# Revit family: Coffee_Table-Capri-Cumberland
name_source: partatom
category: Furniture
revit_build: Autodesk Revit 2014 (Build: 20130308_1515(x64)
units: mm (PartAtom-declared; Revit-internal decimal feet)

## types (5) — shared parameters
Assembly Code = E2020200
Base Finish = CUM - Powder Coat - Metal White
Glide Finish = CUM - Plastic Black
Keynote = 12500
Leg Finish = CUM - Powder Coat - Metal White
Low Emitting Finish = Yes
Low Emitting Material = Yes
Manufacturer = Cumberland Furniture
Post Finish = CUM - Powder Coat - Metal White
Salvage or Reuse = Yes
Type Comments = Capri
URL = www.cumberlandfurniture.com
zero-valued in all types: Percentage of Recycled Content

## per-type parameters (varying)
| type | Description | Diameter | Height | Leg Spread | Leg W | Plus Base | Post Dia | RH1 | RH2 | RV1 | RV2 | Rad-H | Rad-V | X Base |
| 3132 | Coffee Table 18" Dia, 20 3/8" H | 18" | 20 3/8" | 15" | 1 1/2" | Yes | 1 1/2" | 8 11/16" | 8 1/4" | 8 11/16" | 8 1/4" | 9" | 9" | No |
| 3133 | Coffee Table  24" Dia, 20 3/8" H | 24" | 20 3/8" | 18" | 1 1/2" | Yes | 1 1/2" | 11 11/16" | 11 1/4" | 11 11/16" | 11 1/4" | 12" | 12" | No |
| 3135 | Occassional Table 24""Dia 28 7/8"" H | 42" | 28 7/8" | 18" | 1 1/2" | Yes | 1 1/2" | 11 11/16" | 11 1/4" | 11 11/16" | 11 1/4" | 12" | 12" | No |
| 3136 | Coffee Table 30" Dia, 20 3/8" H | 30" | 20 3/8" | 24" | 2" | Yes | 2" | 14 11/16" | 14 1/4" | 14 11/16" | 14 1/4" | 15" | 15" | No |
| 3134 | Coffee Table  24"" Ellipse - Dia 30x15"" H | 24" | 20 3/8" | 18" | 1 1/2" | No | 1 1/2" | 11 11/16" | 11 1/4" | 6 11/16" | 6 1/4" | 12" | 7" | Yes |

note: column(s) folded — value = type name in every type: Model

## geometry (parser evidence)
native form markers: Sweep x7
no freeform markers — native parametric forms only
